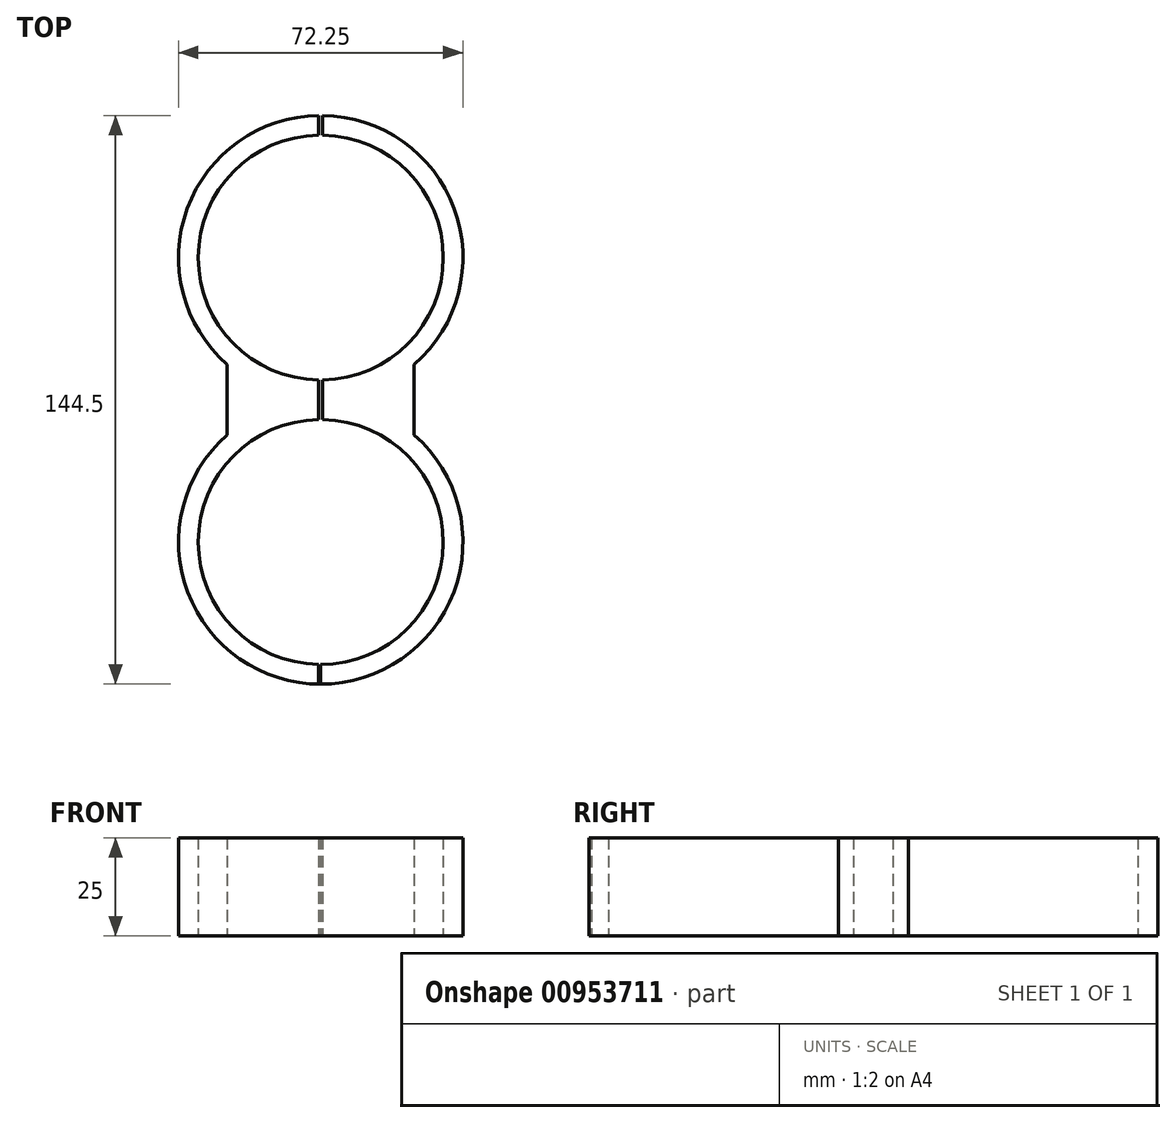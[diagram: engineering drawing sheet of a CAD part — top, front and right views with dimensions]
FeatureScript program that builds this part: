
annotation { "Feature Type Name" : "Feature", "Feature Type Description" : "" }
export const myFeature = defineFeature(function(context is Context, id is Id, definition is map)
    precondition{}
    {
        {
            var Q0;
            Q0=qCreatedBy(makeId("Top.planeOp"),FACE);
            var sketch = newSketch(context, id + "F0", { "sketchPlane" : qUnion([Q0])});
            skArc(sketch, "E0", {"start": v(-0.5, 58.34) * mm, "mid": v(0, -3.9) * mm, "end": v(0.5, 58.34) * mm});
            skArc(sketch, "E1.0", {"start": v(-0.5, 63.34) * mm, "mid": v(0, -8.9) * mm, "end": v(0.5, 63.34) * mm});
            skCircle(sketch, "E2", {"center": v(0, -45.03) * mm, "radius": 31.12 * mm});
            skCircle(sketch, "E3.0", {"center": v(0, -45.03) * mm, "radius": 36.12 * mm});
            skLineSegment(sketch, "E4", {"start": v(-23.76, 0) * mm, "end": v(-23.76, -17.82) * mm});
            skLineSegment(sketch, "E5.MirrorCS", {"start": v(23.76, 0) * mm, "end": v(23.76, -17.82) * mm});
            skLineSegment(sketch, "E6.trimOffspring", {"start": v(0, -3.9) * mm, "end": v(0, -13.9) * mm});
            skLineSegment(sketch, "E7.trimOffspring", {"start": v(0, -76.16) * mm, "end": v(0, -84.62) * mm});
            skPoint(sketch, "E8.orphan", {"position": v(0, 69.83) * mm});
            skLineSegment(sketch, "E9.top", {"start": v(0, -80.55) * mm, "end": v(-0.5, -80.55) * mm});
            skLineSegment(sketch, "E9.left", {"start": v(0, 67.94) * mm, "end": v(0, -80.55) * mm});
            skLineSegment(sketch, "E9.right", {"start": v(-0.5, 67.94) * mm, "end": v(-0.5, -80.55) * mm});
            skLineSegment(sketch, "E10.MirrorCS", {"start": v(0.5, 67.94) * mm, "end": v(0.5, -80.55) * mm});
            skSolve(sketch);
        }
        {
            var Q0;
            {var subQ0=sQuery(id+"F0.wireOp",EDGE,"E10.MirrorCS");var subQ1=sQuery(id+"F0.wireOp",EDGE,"E0");var subQ2=makeQuery(id+"F0.imprint","INTERSECT",VERTEX,{"disambiguationData":[OD(0.0)],"derivedFrom":[subQ1,subQ0]});Q0=makeQuery(id+"F0.imprint","IMPRINT",FACE,{"disambiguationData":[TD([[makeQuery(id+"F0.imprint","IMPRINT",EDGE,{"disambiguationData":[TD([[subQ2,1.0]])],"derivedFrom":subQ1}),-1.0]])]});}
            var Q1;
            {var subQ0=sQuery(id+"F0.wireOp",EDGE,"E9.right");var subQ4=sQuery(id+"F0.wireOp",EDGE,"E0");var subQ5=makeQuery(id+"F0.imprint","INTERSECT",VERTEX,{"disambiguationData":[OD(0.0)],"derivedFrom":[subQ4,subQ0]});Q1=makeQuery(id+"F0.imprint","IMPRINT",FACE,{"disambiguationData":[TD([[makeQuery(id+"F0.imprint","IMPRINT",EDGE,{"disambiguationData":[TD([[subQ5,-1.0]])],"derivedFrom":subQ4}),-1.0]])]});}
            var Q2;
            {var subQ4=sQuery(id+"F0.wireOp",EDGE,"E9.top");Q2=makeQuery(id+"F0.imprint","IMPRINT",FACE,{"disambiguationData":[TD([[makeQuery(id+"F0.imprint","IMPRINT",EDGE,{"derivedFrom":subQ4}),1.0]])]});}
            var Q3;
            {var subQ4=sQuery(id+"F0.wireOp",EDGE,"E10.MirrorCS");var subQ6=sQuery(id+"F0.wireOp",EDGE,"E2");var subQ7=makeQuery(id+"F0.imprint","INTERSECT",VERTEX,{"disambiguationData":[OD(0.0)],"derivedFrom":[subQ6,subQ4]});Q3=makeQuery(id+"F0.imprint","IMPRINT",FACE,{"disambiguationData":[TD([[makeQuery(id+"F0.imprint","IMPRINT",EDGE,{"disambiguationData":[TD([[subQ7,1.0]])],"derivedFrom":subQ6}),-1.0]])]});}
            var Q4;
            {var subQ0=sQuery(id+"F0.wireOp",EDGE,"E5.MirrorCS");Q4=makeQuery(id+"F0.imprint","IMPRINT",FACE,{"disambiguationData":[TD([[makeQuery(id+"F0.imprint","IMPRINT",EDGE,{"derivedFrom":subQ0}),-1.0]])]});}
            var Q5;
            {var subQ0=sQuery(id+"F0.wireOp",EDGE,"E4");Q5=makeQuery(id+"F0.imprint","IMPRINT",FACE,{"disambiguationData":[TD([[makeQuery(id+"F0.imprint","IMPRINT",EDGE,{"derivedFrom":subQ0}),1.0]])]});}
            extrude(context, id + "F1", {"entities" : qUnion([Q0, Q1, Q2, Q3, Q4, Q5]), "depth" : 25 * mm, "offsetDistance" : 25 * mm});
        }
    });
